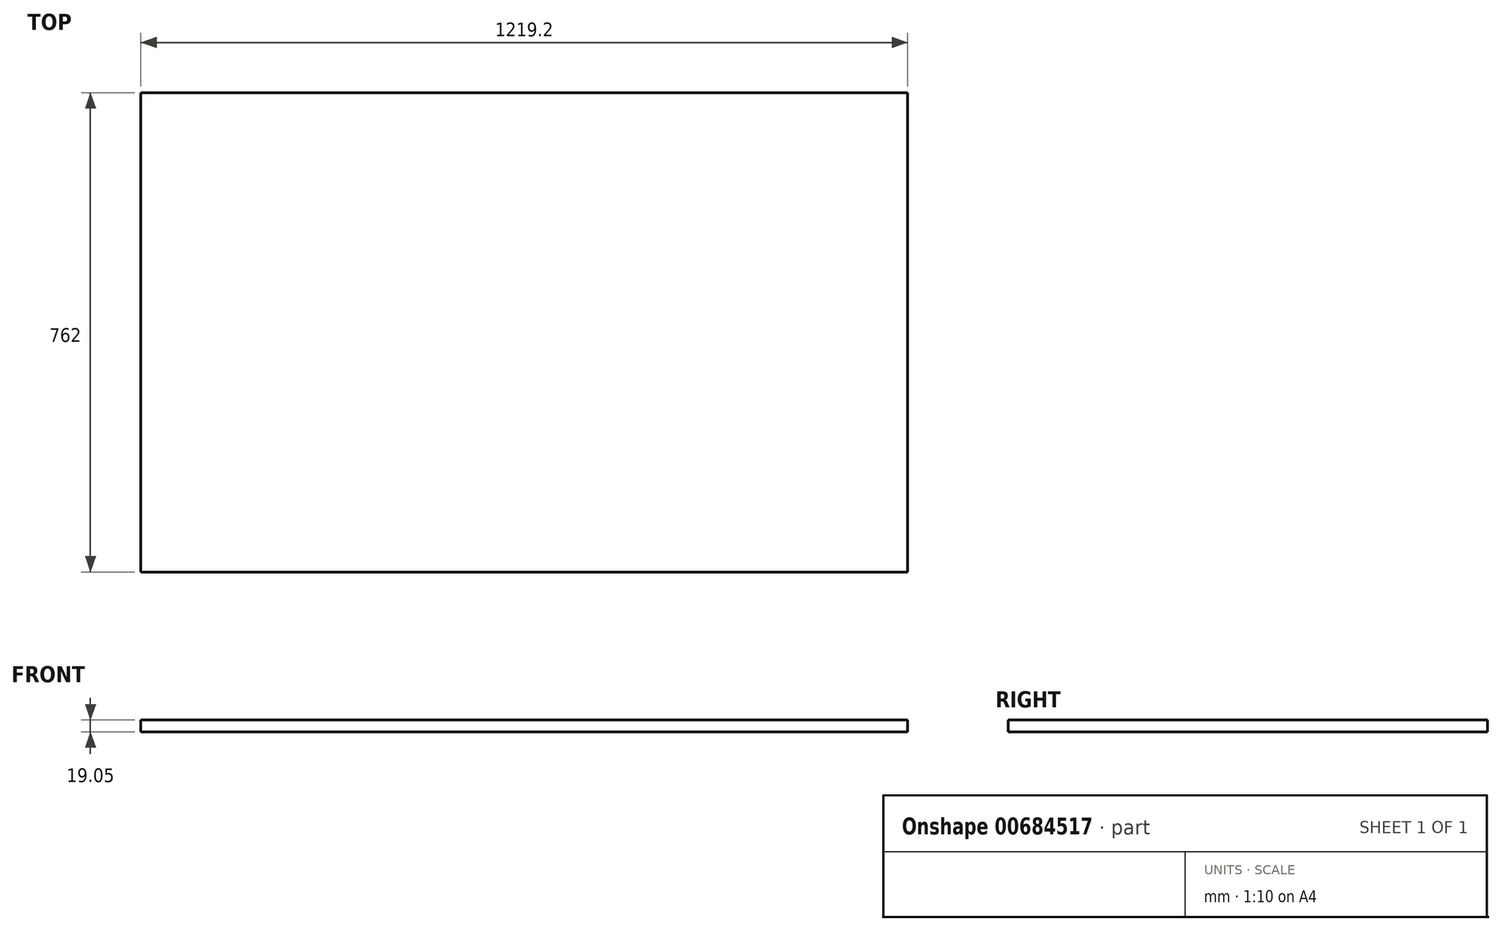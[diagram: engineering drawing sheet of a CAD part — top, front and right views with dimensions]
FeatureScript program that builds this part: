
annotation { "Feature Type Name" : "Feature", "Feature Type Description" : "" }
export const myFeature = defineFeature(function(context is Context, id is Id, definition is map)
    precondition{}
    {
        {
            var Q0;
            Q0=qCreatedBy(makeId("Top.planeOp"),FACE);
            var sketch = newSketch(context, id + "F0", { "sketchPlane" : qUnion([Q0])});
            skLineSegment(sketch, "E0.bottom", {"start": v(-608.83, 406.68) * mm, "end": v(610.37, 406.68) * mm});
            skLineSegment(sketch, "E0.top", {"start": v(-608.83, -355.32) * mm, "end": v(610.37, -355.32) * mm});
            skLineSegment(sketch, "E0.left", {"start": v(-608.83, 406.68) * mm, "end": v(-608.83, -355.32) * mm});
            skLineSegment(sketch, "E0.right", {"start": v(610.37, 406.68) * mm, "end": v(610.37, -355.32) * mm});
            skSolve(sketch);
        }
        {
            var Q0;
            Q0 = qSketchRegion(id + "F0", true);
            extrude(context, id + "F1", {"entities" : qUnion([Q0]), "depth" : 19.05 * mm, "offsetDistance" : 25.4 * mm});
        }
    });
